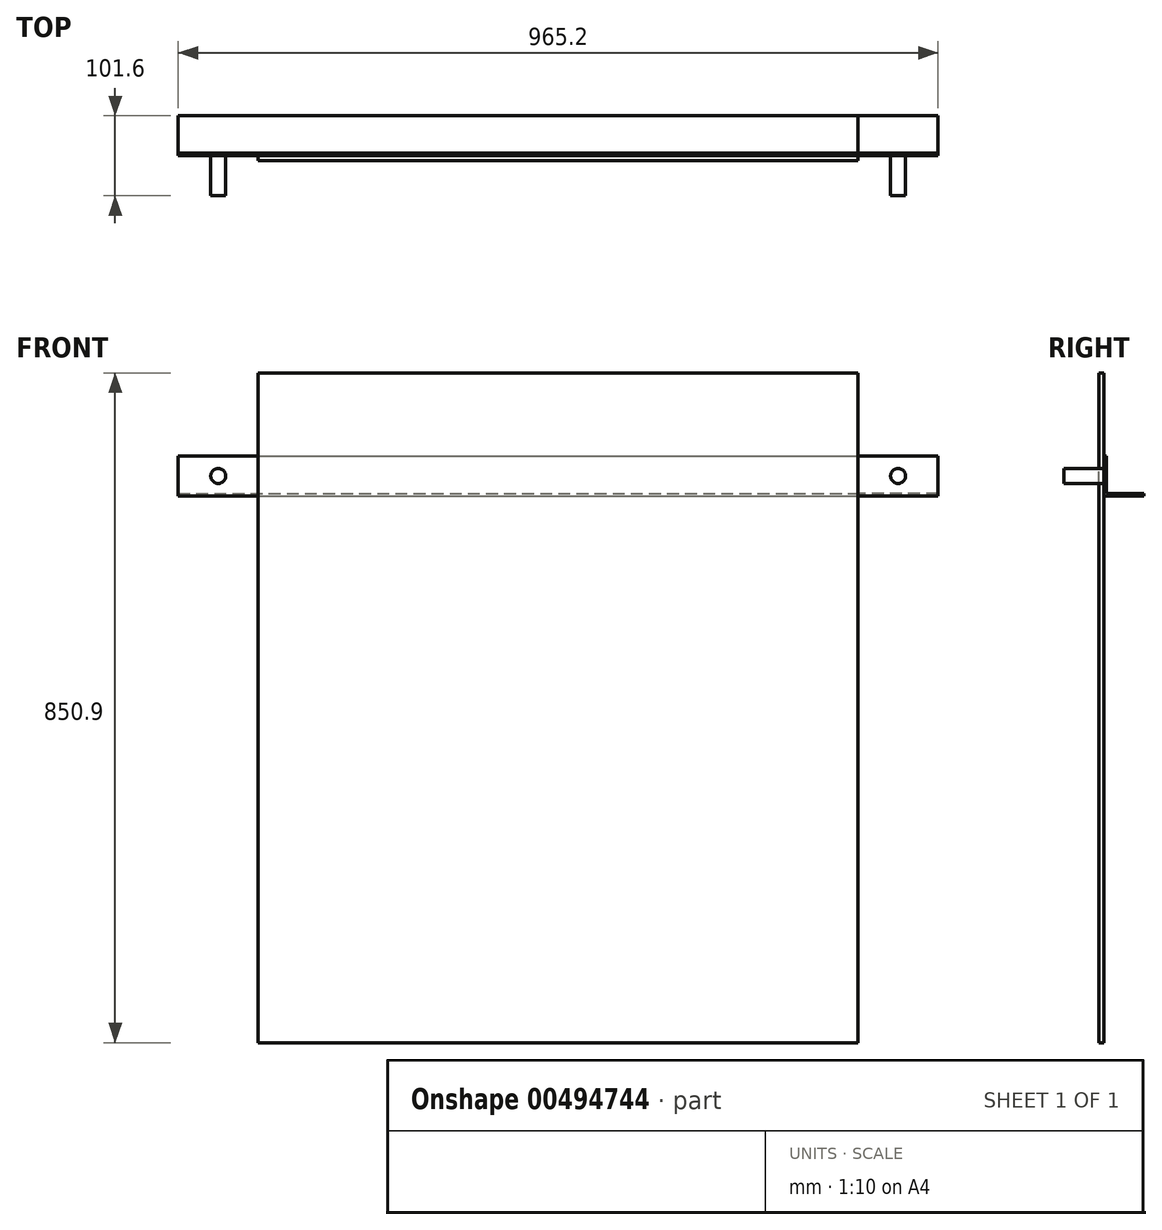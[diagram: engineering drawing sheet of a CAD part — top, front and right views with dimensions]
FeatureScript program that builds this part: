
annotation { "Feature Type Name" : "Feature", "Feature Type Description" : "" }
export const myFeature = defineFeature(function(context is Context, id is Id, definition is map)
    precondition{}
    {
        {
            var Q0;
            Q0=qCreatedBy(makeId("Front.planeOp"),FACE);
            var sketch = newSketch(context, id + "F0", { "sketchPlane" : qUnion([Q0])});
            skLineSegment(sketch, "E0.bottom", {"start": v(0, 0) * mm, "end": v(762, 0) * mm});
            skLineSegment(sketch, "E0.top", {"start": v(0, 850.9) * mm, "end": v(762, 850.9) * mm});
            skLineSegment(sketch, "E0.left", {"start": v(0, 0) * mm, "end": v(0, 850.9) * mm});
            skLineSegment(sketch, "E0.right", {"start": v(762, 0) * mm, "end": v(762, 850.9) * mm});
            skSolve(sketch);
        }
        {
            var Q0;
            Q0 = qSketchRegion(id + "F0", true);
            extrude(context, id + "F1", {"entities" : qUnion([Q0]), "depth" : 6.35 * mm});
        }
        {
            var Q0;
            Q0=makeQuery(id+"F1.opExtrude","SWEPT_FACE",FACE,{"disambiguationData":[OSD([sQuery(id+"F0.wireOp",EDGE,"E0.right")])]});
            var sketch = newSketch(context, id + "F2", { "sketchPlane" : qUnion([Q0])});
            skLineSegment(sketch, "E1", {"start": v(0, 623.46) * mm, "end": v(0, 674.26) * mm});
            skLineSegment(sketch, "E2", {"start": v(0, 674.26) * mm, "end": v(50.8, 674.26) * mm});
            skLineSegment(sketch, "E3", {"start": v(50.8, 674.26) * mm, "end": v(50.8, 671.08) * mm});
            skLineSegment(sketch, "E4", {"start": v(50.8, 671.08) * mm, "end": v(3.17, 671.08) * mm});
            skLineSegment(sketch, "E5", {"start": v(3.17, 671.08) * mm, "end": v(3.17, 623.46) * mm});
            skLineSegment(sketch, "E6", {"start": v(0, 623.46) * mm, "end": v(3.17, 623.46) * mm});
            skSolve(sketch);
        }
        {
            var Q0;
            Q0 = qSketchRegion(id + "F2", true);
            extrude(context, id + "F3", {"entities" : qUnion([Q0]), "depth" : 101.6 * mm});
        }
        {
            var Q0;
            Q0 = qSketchRegion(id + "F2", true);
            extrude(context, id + "F4", {"entities" : qUnion([Q0]), "oppositeDirection" : true, "depth" : 863.6 * mm});
        }
        {
            var Q0;
            Q0=makeQuery(id+"F3.opExtrude","SWEPT_FACE",FACE,{"disambiguationData":[OSD([sQuery(id+"F2.wireOp",EDGE,"E1")])]});
            var sketch = newSketch(context, id + "F5", { "sketchPlane" : qUnion([Q0])});
            skCircle(sketch, "E7", {"center": v(812.8, 648.86) * mm, "radius": 9.53 * mm});
            skPoint(sketch, "E7.centerSnap0", {"position": v(762, 648.86) * mm});
            skSolve(sketch);
        }
        {
            var Q0;
            Q0 = qSketchRegion(id + "F5", true);
            extrude(context, id + "F6", {"entities" : qUnion([Q0]), "operationType" : NewBodyOperationType.ADD, "depth" : 50.8 * mm});
        }
        {
            var Q0;
            Q0=makeQuery(id+"F4.opExtrude","SWEPT_FACE",FACE,{"disambiguationData":[OSD([sQuery(id+"F2.wireOp",EDGE,"E1")])]});
            var sketch = newSketch(context, id + "F7", { "sketchPlane" : qUnion([Q0])});
            skCircle(sketch, "E8", {"center": v(-50.8, 648.86) * mm, "radius": 9.53 * mm});
            skSolve(sketch);
        }
        {
            var Q0;
            Q0 = qSketchRegion(id + "F7", true);
            extrude(context, id + "F8", {"entities" : qUnion([Q0]), "operationType" : NewBodyOperationType.ADD, "depth" : 50.8 * mm});
        }
        {
            var Q0;
            Q0=makeQuery(id+"F4.opExtrude","SWEPT_BODY",BODY,{"disambiguationData":[OSD([sQuery(id+"F2.wireOp",EDGE,"E1"),sQuery(id+"F2.wireOp",EDGE,"E2"),sQuery(id+"F2.wireOp",EDGE,"E3"),sQuery(id+"F2.wireOp",EDGE,"E4"),sQuery(id+"F2.wireOp",EDGE,"E5"),sQuery(id+"F2.wireOp",EDGE,"E6")])]});
            var Q1;
            Q1=makeQuery(id+"F3.opExtrude","SWEPT_BODY",BODY,{"disambiguationData":[OSD([sQuery(id+"F2.wireOp",EDGE,"E1"),sQuery(id+"F2.wireOp",EDGE,"E2"),sQuery(id+"F2.wireOp",EDGE,"E3"),sQuery(id+"F2.wireOp",EDGE,"E4"),sQuery(id+"F2.wireOp",EDGE,"E5"),sQuery(id+"F2.wireOp",EDGE,"E6")])]});
            deleteBodies(context, id + "F9", {"entities" : qUnion([Q0, Q1])});
        }
        {
            var Q0;
            Q0=makeQuery(id+"F1.opExtrude","SWEPT_FACE",FACE,{"disambiguationData":[OSD([sQuery(id+"F0.wireOp",EDGE,"E0.right")])]});
            var sketch = newSketch(context, id + "F10", { "sketchPlane" : qUnion([Q0])});
            skLineSegment(sketch, "E9", {"start": v(0, 694.5) * mm, "end": v(50.8, 694.5) * mm});
            skLineSegment(sketch, "E10", {"start": v(50.8, 694.5) * mm, "end": v(50.8, 697.68) * mm});
            skLineSegment(sketch, "E11", {"start": v(50.8, 697.68) * mm, "end": v(3.18, 697.68) * mm});
            skLineSegment(sketch, "E12", {"start": v(3.18, 697.68) * mm, "end": v(3.18, 745.3) * mm});
            skLineSegment(sketch, "E13", {"start": v(3.18, 745.3) * mm, "end": v(0, 745.3) * mm});
            skLineSegment(sketch, "E14", {"start": v(0, 745.3) * mm, "end": v(0, 694.5) * mm});
            skSolve(sketch);
        }
        {
            var Q0;
            Q0 = qSketchRegion(id + "F10", true);
            extrude(context, id + "F11", {"entities" : qUnion([Q0]), "depth" : 101.6 * mm});
        }
        {
            var Q0;
            Q0 = qSketchRegion(id + "F10", true);
            extrude(context, id + "F12", {"entities" : qUnion([Q0]), "oppositeDirection" : true, "depth" : 863.6 * mm});
        }
        {
            var Q0;
            Q0=makeQuery(id+"F11.opExtrude","SWEPT_FACE",FACE,{"disambiguationData":[OSD([sQuery(id+"F10.wireOp",EDGE,"E14")])]});
            var sketch = newSketch(context, id + "F13", { "sketchPlane" : qUnion([Q0])});
            skCircle(sketch, "E15", {"center": v(812.8, 719.9) * mm, "radius": 9.53 * mm});
            skPoint(sketch, "E15.centerSnap0", {"position": v(762, 719.9) * mm});
            skSolve(sketch);
        }
        {
            var Q0;
            Q0 = qSketchRegion(id + "F13", true);
            extrude(context, id + "F14", {"entities" : qUnion([Q0]), "operationType" : NewBodyOperationType.ADD, "depth" : 50.8 * mm});
        }
        {
            var Q0;
            Q0=makeQuery(id+"F12.opExtrude","SWEPT_FACE",FACE,{"disambiguationData":[OSD([sQuery(id+"F10.wireOp",EDGE,"E14")])]});
            var sketch = newSketch(context, id + "F15", { "sketchPlane" : qUnion([Q0])});
            skCircle(sketch, "E16", {"center": v(-50.8, 719.9) * mm, "radius": 9.53 * mm});
            skSolve(sketch);
        }
        {
            var Q0;
            Q0 = qSketchRegion(id + "F15", true);
            extrude(context, id + "F16", {"entities" : qUnion([Q0]), "operationType" : NewBodyOperationType.ADD, "depth" : 50.8 * mm});
        }
    });
